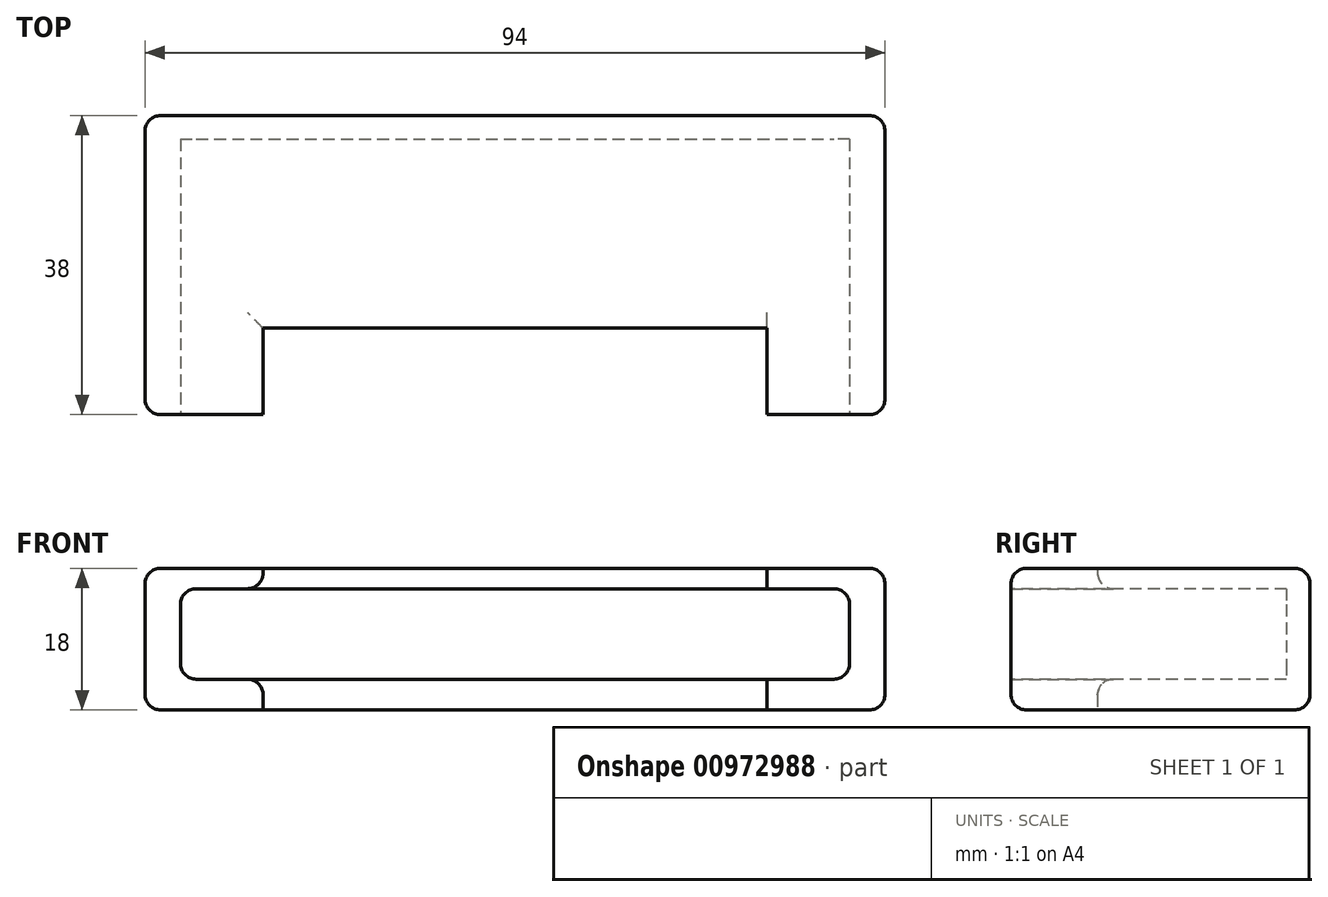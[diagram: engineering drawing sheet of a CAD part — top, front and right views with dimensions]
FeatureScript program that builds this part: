
annotation { "Feature Type Name" : "Feature", "Feature Type Description" : "" }
export const myFeature = defineFeature(function(context is Context, id is Id, definition is map)
    precondition{}
    {
        {
            var Q0;
            Q0=qCreatedBy(makeId("Top.planeOp"),FACE);
            var sketch = newSketch(context, id + "F0", { "sketchPlane" : qUnion([Q0])});
            skLineSegment(sketch, "E0", {"start": v(0, 35) * mm, "end": v(-42.5, 35) * mm});
            skLineSegment(sketch, "E1", {"start": v(-42.5, 35) * mm, "end": v(-42.5, 0) * mm});
            skLineSegment(sketch, "E2", {"start": v(-42.5, 0) * mm, "end": v(0, 0) * mm});
            skLineSegment(sketch, "E3.MirrorCS", {"start": v(0, 35) * mm, "end": v(42.5, 35) * mm});
            skLineSegment(sketch, "E4.MirrorCS", {"start": v(42.5, 35) * mm, "end": v(42.5, 0) * mm});
            skLineSegment(sketch, "E5.MirrorCS", {"start": v(42.5, 0) * mm, "end": v(0, 0) * mm});
            skSolve(sketch);
        }
        {
            var Q0;
            Q0=qCreatedBy(makeId("Top.planeOp"),FACE);
            var sketch = newSketch(context, id + "F1", { "sketchPlane" : qUnion([Q0])});
            skLineSegment(sketch, "E6", {"start": v(-47, 38) * mm, "end": v(-47, 0) * mm});
            skLineSegment(sketch, "E7", {"start": v(-47, 0) * mm, "end": v(-32, 0) * mm});
            skLineSegment(sketch, "E8", {"start": v(-32, 0) * mm, "end": v(-32, 11) * mm});
            skLineSegment(sketch, "E9", {"start": v(-32, 11) * mm, "end": v(0, 11) * mm});
            skLineSegment(sketch, "E10", {"start": v(-47, 38) * mm, "end": v(0, 38) * mm});
            skLineSegment(sketch, "E11.MirrorCS", {"start": v(47, 38) * mm, "end": v(47, 0) * mm});
            skLineSegment(sketch, "E12.MirrorCS", {"start": v(47, 0) * mm, "end": v(32, 0) * mm});
            skLineSegment(sketch, "E13.MirrorCS", {"start": v(32, 0) * mm, "end": v(32, 11) * mm});
            skLineSegment(sketch, "E14.MirrorCS", {"start": v(47, 38) * mm, "end": v(0, 38) * mm});
            skLineSegment(sketch, "E15.MirrorCS", {"start": v(32, 11) * mm, "end": v(0, 11) * mm});
            skSolve(sketch);
        }
        {
            var Q0;
            Q0 = qSketchRegion(id + "F1", true);
            extrude(context, id + "F2", {"entities" : qUnion([Q0]), "depth" : 18 * mm, "offsetDistance" : 25 * mm});
        }
        {
            var Q0;
            Q0 = qSketchRegion(id + "F0", true);
            extrude(context, id + "F3", {"entities" : qUnion([Q0]), "operationType" : NewBodyOperationType.REMOVE, "depth" : 15.4 * mm, "offsetDistance" : 25 * mm, "hasSecondDirection" : true, "secondDirectionOppositeDirection" : false, "secondDirectionDepth" : 3.9 * mm});
        }
        {
            var Q0;
            Q0=makeQuery(id+"F2.opExtrude","SWEPT_EDGE",EDGE,{"disambiguationData":[OSD([sQuery(id+"F1.wireOp",EDGE,"E6"),sQuery(id+"F1.wireOp",EDGE,"E10")])]});
            var Q1;
            Q1=makeQuery(id+"F2.opExtrude","SWEPT_EDGE",EDGE,{"disambiguationData":[OSD([sQuery(id+"F1.wireOp",EDGE,"E11.MirrorCS"),sQuery(id+"F1.wireOp",EDGE,"E14.MirrorCS")])]});
            var Q2;
            Q2=makeQuery(id+"F2.opExtrude","SWEPT_EDGE",EDGE,{"disambiguationData":[OSD([sQuery(id+"F1.wireOp",EDGE,"E11.MirrorCS"),sQuery(id+"F1.wireOp",EDGE,"E12.MirrorCS")])]});
            var Q3;
            Q3=makeQuery(id+"F2.opExtrude","SWEPT_EDGE",EDGE,{"disambiguationData":[OSD([sQuery(id+"F1.wireOp",EDGE,"E6"),sQuery(id+"F1.wireOp",EDGE,"E7")])]});
            var Q4;
            {var subQ0=sQuery(id+"F0.wireOp",EDGE,"E5.MirrorCS");var subQ1=sQuery(id+"F0.wireOp",EDGE,"E2");Q4=makeQuery(id+"F3.boolean.opBoolean","COPY",EDGE,{"disambiguationData":[topologyDisambiguationEdgeConnected([makeQuery(id+"F2.opExtrude","SWEPT_FACE",FACE,{"disambiguationData":[OSD([sQuery(id+"F1.wireOp",EDGE,"E7")])]})])],"derivedFrom":makeQuery(id+"F3.opExtrude","CAP_EDGE",EDGE,{"disambiguationData":[OSD([subQ1,subQ0])],"isStart":true})});}
            var Q5;
            Q5=makeQuery(id+"F3.boolean.opBoolean","INTERSECT",EDGE,{"derivedFrom":[makeQuery(id+"F2.opExtrude","SWEPT_FACE",FACE,{"disambiguationData":[OSD([sQuery(id+"F1.wireOp",EDGE,"E8")])]}),makeQuery(id+"F3.opExtrude","CAP_FACE",FACE,{"disambiguationData":[OSD([sQuery(id+"F0.wireOp",EDGE,"E0"),sQuery(id+"F0.wireOp",EDGE,"E1"),sQuery(id+"F0.wireOp",EDGE,"E2"),sQuery(id+"F0.wireOp",EDGE,"E3.MirrorCS"),sQuery(id+"F0.wireOp",EDGE,"E4.MirrorCS"),sQuery(id+"F0.wireOp",EDGE,"E5.MirrorCS")])],"isStart":true})]});
            var Q6;
            {var subQ0=sQuery(id+"F0.wireOp",EDGE,"E5.MirrorCS");var subQ1=sQuery(id+"F0.wireOp",EDGE,"E2");Q6=makeQuery(id+"F3.boolean.opBoolean","COPY",EDGE,{"disambiguationData":[topologyDisambiguationEdgeConnected([makeQuery(id+"F2.opExtrude","SWEPT_FACE",FACE,{"disambiguationData":[OSD([sQuery(id+"F1.wireOp",EDGE,"E7")])]})])],"derivedFrom":makeQuery(id+"F3.opExtrude","CAP_EDGE",EDGE,{"disambiguationData":[OSD([subQ1,subQ0])],"isStart":false})});}
            var Q7;
            Q7=makeQuery(id+"F3.boolean.opBoolean","COPY",EDGE,{"derivedFrom":makeQuery(id+"F3.opExtrude","CAP_EDGE",EDGE,{"disambiguationData":[OSD([sQuery(id+"F0.wireOp",EDGE,"E1")])],"isStart":false})});
            var Q8;
            Q8=makeQuery(id+"F3.boolean.opBoolean","INTERSECT",EDGE,{"derivedFrom":[makeQuery(id+"F2.opExtrude","SWEPT_FACE",FACE,{"disambiguationData":[OSD([sQuery(id+"F1.wireOp",EDGE,"E8")])]}),makeQuery(id+"F3.opExtrude","CAP_FACE",FACE,{"disambiguationData":[OSD([sQuery(id+"F0.wireOp",EDGE,"E0"),sQuery(id+"F0.wireOp",EDGE,"E1"),sQuery(id+"F0.wireOp",EDGE,"E2"),sQuery(id+"F0.wireOp",EDGE,"E3.MirrorCS"),sQuery(id+"F0.wireOp",EDGE,"E4.MirrorCS"),sQuery(id+"F0.wireOp",EDGE,"E5.MirrorCS")])],"isStart":false})]});
            var Q9;
            Q9=makeQuery(id+"F3.boolean.opBoolean","INTERSECT",EDGE,{"derivedFrom":[makeQuery(id+"F2.opExtrude","SWEPT_FACE",FACE,{"disambiguationData":[OSD([sQuery(id+"F1.wireOp",EDGE,"E9"),sQuery(id+"F1.wireOp",EDGE,"E15.MirrorCS")])]}),makeQuery(id+"F3.opExtrude","CAP_FACE",FACE,{"disambiguationData":[OSD([sQuery(id+"F0.wireOp",EDGE,"E0"),sQuery(id+"F0.wireOp",EDGE,"E1"),sQuery(id+"F0.wireOp",EDGE,"E2"),sQuery(id+"F0.wireOp",EDGE,"E3.MirrorCS"),sQuery(id+"F0.wireOp",EDGE,"E4.MirrorCS"),sQuery(id+"F0.wireOp",EDGE,"E5.MirrorCS")])],"isStart":false})]});
            var Q10;
            {var subQ0=sQuery(id+"F0.wireOp",EDGE,"E5.MirrorCS");var subQ1=sQuery(id+"F0.wireOp",EDGE,"E2");Q10=makeQuery(id+"F3.boolean.opBoolean","COPY",EDGE,{"disambiguationData":[topologyDisambiguationEdgeConnected([makeQuery(id+"F2.opExtrude","SWEPT_FACE",FACE,{"disambiguationData":[OSD([sQuery(id+"F1.wireOp",EDGE,"E12.MirrorCS")])]})])],"derivedFrom":makeQuery(id+"F3.opExtrude","CAP_EDGE",EDGE,{"disambiguationData":[OSD([subQ1,subQ0])],"isStart":false})});}
            var Q11;
            Q11=makeQuery(id+"F3.boolean.opBoolean","COPY",EDGE,{"derivedFrom":makeQuery(id+"F3.opExtrude","SWEPT_EDGE",EDGE,{"disambiguationData":[OSD([sQuery(id+"F0.wireOp",EDGE,"E4.MirrorCS"),sQuery(id+"F0.wireOp",EDGE,"E5.MirrorCS")])]})});
            var Q12;
            {var subQ0=sQuery(id+"F0.wireOp",EDGE,"E5.MirrorCS");var subQ1=sQuery(id+"F0.wireOp",EDGE,"E2");Q12=makeQuery(id+"F3.boolean.opBoolean","COPY",EDGE,{"disambiguationData":[topologyDisambiguationEdgeConnected([makeQuery(id+"F2.opExtrude","SWEPT_FACE",FACE,{"disambiguationData":[OSD([sQuery(id+"F1.wireOp",EDGE,"E12.MirrorCS")])]})])],"derivedFrom":makeQuery(id+"F3.opExtrude","CAP_EDGE",EDGE,{"disambiguationData":[OSD([subQ1,subQ0])],"isStart":true})});}
            var Q13;
            Q13=makeQuery(id+"F3.boolean.opBoolean","INTERSECT",EDGE,{"derivedFrom":[makeQuery(id+"F2.opExtrude","SWEPT_FACE",FACE,{"disambiguationData":[OSD([sQuery(id+"F1.wireOp",EDGE,"E9"),sQuery(id+"F1.wireOp",EDGE,"E15.MirrorCS")])]}),makeQuery(id+"F3.opExtrude","CAP_FACE",FACE,{"disambiguationData":[OSD([sQuery(id+"F0.wireOp",EDGE,"E0"),sQuery(id+"F0.wireOp",EDGE,"E1"),sQuery(id+"F0.wireOp",EDGE,"E2"),sQuery(id+"F0.wireOp",EDGE,"E3.MirrorCS"),sQuery(id+"F0.wireOp",EDGE,"E4.MirrorCS"),sQuery(id+"F0.wireOp",EDGE,"E5.MirrorCS")])],"isStart":true})]});
            fillet(context, id + "F4", {"entities" : qUnion([Q0, Q1, Q2, Q3, Q4, Q5, Q6, Q7, Q8, Q9, Q10, Q11, Q12, Q13]), "radius" : 2 * mm, "tangentPropagation" : true, "allowEdgeOverflow" : false});
        }
        {
            var Q0;
            Q0=makeQuery(id+"F2.opExtrude","CAP_EDGE",EDGE,{"disambiguationData":[OSD([sQuery(id+"F1.wireOp",EDGE,"E6")])],"isStart":true});
            var Q1;
            Q1=makeQuery(id+"F2.opExtrude","CAP_EDGE",EDGE,{"disambiguationData":[OSD([sQuery(id+"F1.wireOp",EDGE,"E6")])],"isStart":false});
            fillet(context, id + "F5", {"entities" : qUnion([Q0, Q1]), "radius" : 2 * mm, "tangentPropagation" : true, "allowEdgeOverflow" : false});
        }
        {
            var Q0;
            Q0=makeQuery(id+"F3.boolean.opBoolean","COPY",EDGE,{"derivedFrom":makeQuery(id+"F3.opExtrude","CAP_EDGE",EDGE,{"disambiguationData":[OSD([sQuery(id+"F0.wireOp",EDGE,"E4.MirrorCS")])],"isStart":false})});
            fillet(context, id + "F6", {"entities" : qUnion([Q0]), "radius" : 2 * mm, "tangentPropagation" : true, "allowEdgeOverflow" : false});
        }
        {
            var Q0;
            Q0=makeQuery(id+"F3.boolean.opBoolean","COPY",EDGE,{"derivedFrom":makeQuery(id+"F3.opExtrude","CAP_EDGE",EDGE,{"disambiguationData":[OSD([sQuery(id+"F0.wireOp",EDGE,"E1")])],"isStart":true})});
            var Q1;
            Q1=makeQuery(id+"F3.boolean.opBoolean","COPY",EDGE,{"derivedFrom":makeQuery(id+"F3.opExtrude","CAP_EDGE",EDGE,{"disambiguationData":[OSD([sQuery(id+"F0.wireOp",EDGE,"E4.MirrorCS")])],"isStart":true})});
            fillet(context, id + "F7", {"entities" : qUnion([Q0, Q1]), "radius" : 2 * mm, "tangentPropagation" : true, "allowEdgeOverflow" : false});
        }
    });
